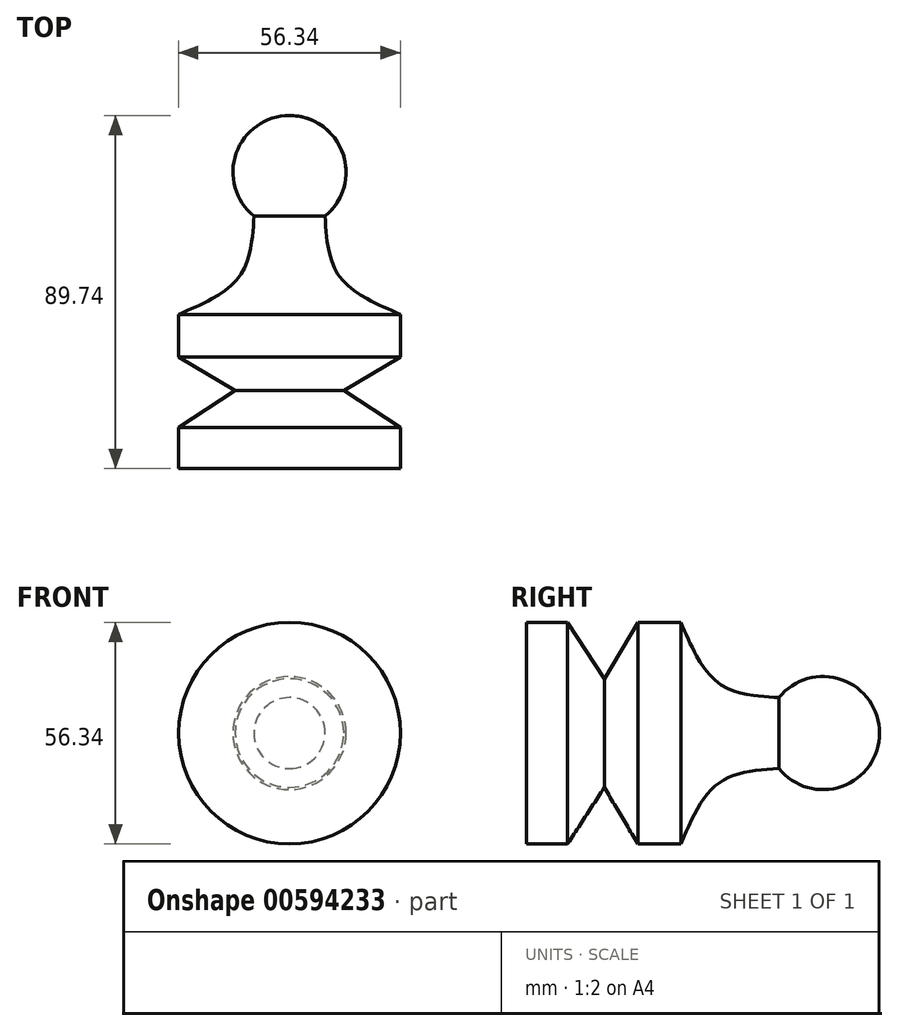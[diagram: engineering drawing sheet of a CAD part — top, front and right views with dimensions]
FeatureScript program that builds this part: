
annotation { "Feature Type Name" : "Feature", "Feature Type Description" : "" }
export const myFeature = defineFeature(function(context is Context, id is Id, definition is map)
    precondition{}
    {
        {
            var Q0;
            Q0=qCreatedBy(makeId("Top.planeOp"),FACE);
            var sketch = newSketch(context, id + "F0", { "sketchPlane" : qUnion([Q0])});
            skLineSegment(sketch, "E0", {"start": v(0, 0) * mm, "end": v(28.17, 0) * mm});
            skLineSegment(sketch, "E1", {"start": v(28.17, 0) * mm, "end": v(28.17, 10.49) * mm});
            skLineSegment(sketch, "E2", {"start": v(13.8, 19.81) * mm, "end": v(28.17, 10.49) * mm});
            skLineSegment(sketch, "E3", {"start": v(13.8, 19.81) * mm, "end": v(28.17, 28.36) * mm});
            skLineSegment(sketch, "E4", {"start": v(28.17, 28.36) * mm, "end": v(28.17, 39.24) * mm});
            skArc(sketch, "E5", {"start": v(9.03, 64.19) * mm, "mid": v(13.55, 80.16) * mm, "end": v(0, 89.74) * mm});
            skFitSpline(sketch, "E6", {"points": [v(28.17, 39.24) * mm, v(12.63, 48.95) * mm, v(9.03, 64.19) * mm], "startDerivative": vector(-35.73, 15.3) * mm, "endDerivative": vector(-2.1, 34.86) * mm});
            skLineSegment(sketch, "E7", {"start": v(0, 0) * mm, "end": v(0, 89.74) * mm});
            skSolve(sketch);
        }
        {
            var Q0;
            Q0 = qSketchRegion(id + "F0", true);
            var Q1;
            Q1=sQuery(id+"F0.wireOp",EDGE,"E7");
            revolve(context, id + "F1", {"entities" : qUnion([Q0]), "axis" : qUnion([Q1]), "revolveType" : RevolveType.FULL});
        }
    });
